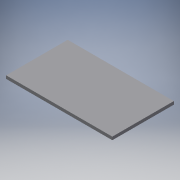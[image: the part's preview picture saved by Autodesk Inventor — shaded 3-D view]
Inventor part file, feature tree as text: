
AUTODESK INVENTOR PART (.ipt)
format: ipt  version: 2018.3 (Build 223284000, 284)  size: 91,648 bytes
history: native  units: mm
features: extrude x1, sketch x1
ambient origin geometry x8: Origin, YZ Plane, XZ Plane, XY Plane, X Axis, Y Axis, Z Axis, Center Point
bodies: Solid1 (feature_tree)
feature tree (2):
  extrude  "Extrusion1"  Depth=20.0mm
  sketch  "Sketch1"  dims[d0=34.5mm d1=20.0mm d2=1.0mm d3=0.0mm]
